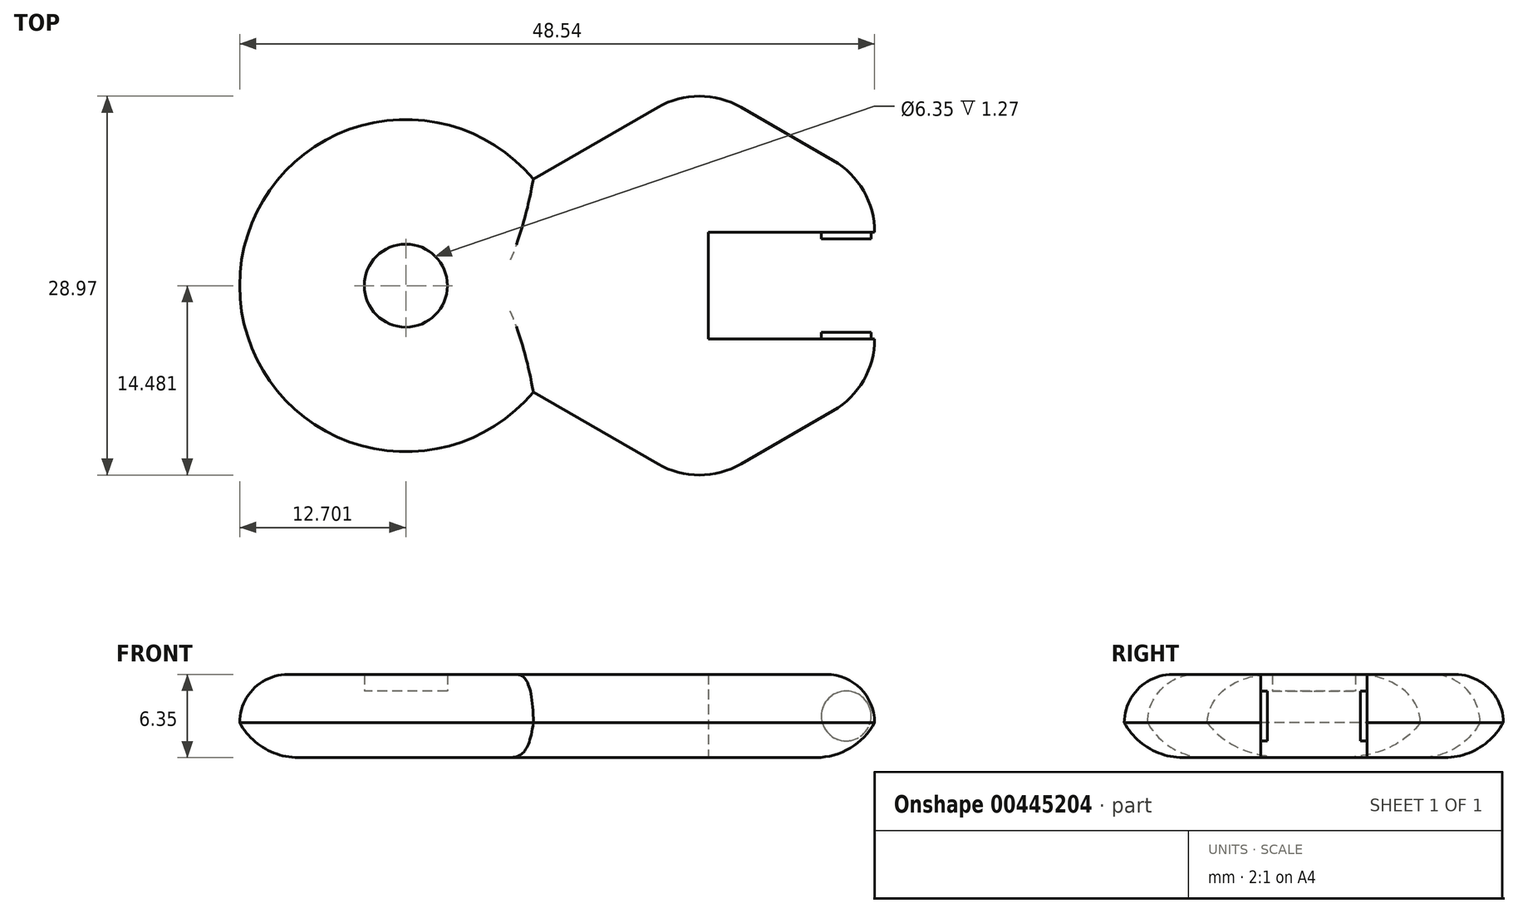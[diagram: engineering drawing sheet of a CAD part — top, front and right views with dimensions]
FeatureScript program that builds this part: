
annotation { "Feature Type Name" : "Feature", "Feature Type Description" : "" }
export const myFeature = defineFeature(function(context is Context, id is Id, definition is map)
    precondition{}
    {
        {
            var Q0;
            Q0=qCreatedBy(makeId("Top.planeOp"),FACE);
            var sketch = newSketch(context, id + "F0", { "sketchPlane" : qUnion([Q0])});
            skArc(sketch, "E0", {"start": v(-23.92, 38.55) * mm, "mid": v(-46.34, 29.5) * mm, "end": v(-22.85, 23.76) * mm});
            skArc(sketch, "E1.cCircle", {"start": v(-22.85, 23.76) * mm, "mid": v(-9.81, 17.1) * mm, "end": v(1.54, 26.34) * mm, "construction": true});
            skLineSegment(sketch, "E1.1", {"start": v(-24.62, 38.14) * mm, "end": v(-14.4, 44.05) * mm});
            skLineSegment(sketch, "E1.2", {"start": v(-8.05, 44.05) * mm, "end": v(-1, 39.98) * mm});
            skLineSegment(sketch, "E1.4", {"start": v(-1, 20.84) * mm, "end": v(-8.05, 16.78) * mm});
            skLineSegment(sketch, "E1.5", {"start": v(-14.4, 16.78) * mm, "end": v(-24.62, 22.68) * mm});
            skPoint(sketch, "E1.0.midPoint", {"position": v(-24.62, 30.41) * mm});
            skPoint(sketch, "E2.visualSharp", {"position": v(-11.22, 45.88) * mm});
            skArc(sketch, "E2.filletArc", {"start": v(-8.05, 44.05) * mm, "mid": v(-11.22, 44.9) * mm, "end": v(-14.4, 44.05) * mm});
            skPoint(sketch, "E3.visualSharp", {"position": v(2.17, 38.14) * mm});
            skArc(sketch, "E3.filletArc", {"start": v(2.17, 34.48) * mm, "mid": v(1.32, 37.65) * mm, "end": v(-1, 39.98) * mm});
            skPoint(sketch, "E4.visualSharp", {"position": v(2.17, 22.68) * mm});
            skArc(sketch, "E4.filletArc", {"start": v(-1, 20.84) * mm, "mid": v(1.32, 23.17) * mm, "end": v(2.17, 26.34) * mm});
            skPoint(sketch, "E5.visualSharp", {"position": v(-11.22, 14.94) * mm});
            skArc(sketch, "E5.filletArc", {"start": v(-14.4, 16.78) * mm, "mid": v(-11.22, 15.93) * mm, "end": v(-8.05, 16.78) * mm});
            skLineSegment(sketch, "E6.bottom", {"start": v(2.17, 34.48) * mm, "end": v(-10.53, 34.48) * mm});
            skLineSegment(sketch, "E6.top", {"start": v(2.17, 26.34) * mm, "end": v(-10.53, 26.34) * mm});
            skLineSegment(sketch, "E6.right", {"start": v(-10.53, 34.48) * mm, "end": v(-10.53, 26.34) * mm});
            skArc(sketch, "E7.trimOffspring", {"start": v(1.54, 34.48) * mm, "mid": v(-9.81, 43.73) * mm, "end": v(-22.85, 37.06) * mm, "construction": true});
            skCircle(sketch, "E8", {"center": v(-33.67, 30.41) * mm, "radius": 3.18 * mm});
            skSolve(sketch);
        }
        {
            var Q0;
            Q0 = qSketchRegion(id + "F0", true);
            extrude(context, id + "F1", {"entities" : qUnion([Q0]), "depth" : 6.35 * mm});
        }
        {
            var Q0;
            Q0=makeQuery(id+"F1.opExtrude","SWEPT_FACE",FACE,{"disambiguationData":[OSD([sQuery(id+"F0.wireOp",EDGE,"E6.top")])]});
            var sketch = newSketch(context, id + "F2", { "sketchPlane" : qUnion([Q0])});
            skCircle(sketch, "E9", {"center": v(0, 3.18) * mm, "radius": 1.9 * mm});
            skPoint(sketch, "E9.centerSnap0", {"position": v(-2.17, 3.18) * mm});
            skSolve(sketch);
        }
        {
            var Q0;
            Q0 = qSketchRegion(id + "F2", true);
            extrude(context, id + "F3", {"entities" : qUnion([Q0]), "operationType" : NewBodyOperationType.ADD, "depth" : 0.5 * mm});
        }
        {
            var Q0;
            Q0=makeQuery(id+"F1.opExtrude","SWEPT_FACE",FACE,{"disambiguationData":[OSD([sQuery(id+"F0.wireOp",EDGE,"E6.bottom")])]});
            var sketch = newSketch(context, id + "F4", { "sketchPlane" : qUnion([Q0])});
            skCircle(sketch, "E10", {"center": v(0, 3.18) * mm, "radius": 1.9 * mm});
            skPoint(sketch, "E10.centerSnap0", {"position": v(2.17, 3.18) * mm});
            skSolve(sketch);
        }
        {
            var Q0;
            Q0 = qSketchRegion(id + "F4", true);
            extrude(context, id + "F5", {"entities" : qUnion([Q0]), "operationType" : NewBodyOperationType.ADD, "depth" : 0.5 * mm});
        }
        {
            var Q0;
            Q0=makeQuery(id+"F0.imprint","IMPRINT",FACE,{"disambiguationData":[TD([[makeQuery(id+"F0.imprint","IMPRINT",EDGE,{"derivedFrom":sQuery(id+"F0.wireOp",EDGE,"E8")}),1.0]])]});
            extrude(context, id + "F6", {"entities" : qUnion([Q0]), "operationType" : NewBodyOperationType.ADD, "depth" : 5.08 * mm});
        }
        {
            var Q0;
            Q0=makeQuery(id+"F1.opExtrude","CAP_EDGE",EDGE,{"disambiguationData":[OSD([sQuery(id+"F0.wireOp",EDGE,"E1.2")])],"isStart":false});
            var Q1;
            Q1=makeQuery(id+"F1.opExtrude","CAP_EDGE",EDGE,{"disambiguationData":[OSD([sQuery(id+"F0.wireOp",EDGE,"E3.filletArc")])],"isStart":false});
            var Q2;
            Q2=makeQuery(id+"F1.opExtrude","CAP_EDGE",EDGE,{"disambiguationData":[OSD([sQuery(id+"F0.wireOp",EDGE,"E0")])],"isStart":false});
            var Q3;
            Q3=makeQuery(id+"F1.opExtrude","CAP_EDGE",EDGE,{"disambiguationData":[OSD([sQuery(id+"F0.wireOp",EDGE,"E1.5")])],"isStart":false});
            fillet(context, id + "F7", {"entities" : qUnion([Q0, Q1, Q2, Q3]), "radius" : 3.68 * mm, "tangentPropagation" : true, "allowEdgeOverflow" : false});
        }
        {
            var Q0;
            Q0=makeQuery(id+"F1.opExtrude","CAP_EDGE",EDGE,{"disambiguationData":[OSD([sQuery(id+"F0.wireOp",EDGE,"E1.1")])],"isStart":true});
            var Q1;
            Q1=makeQuery(id+"F1.opExtrude","CAP_EDGE",EDGE,{"disambiguationData":[OSD([sQuery(id+"F0.wireOp",EDGE,"E2.filletArc")])],"isStart":true});
            var Q2;
            Q2=makeQuery(id+"F1.opExtrude","CAP_EDGE",EDGE,{"disambiguationData":[OSD([sQuery(id+"F0.wireOp",EDGE,"E0")])],"isStart":true});
            var Q3;
            Q3=makeQuery(id+"F1.opExtrude","CAP_EDGE",EDGE,{"disambiguationData":[OSD([sQuery(id+"F0.wireOp",EDGE,"E1.4")])],"isStart":true});
            fillet(context, id + "F8", {"entities" : qUnion([Q0, Q1, Q2, Q3]), "radius" : 5.08 * mm, "tangentPropagation" : true, "allowEdgeOverflow" : false});
        }
    });
